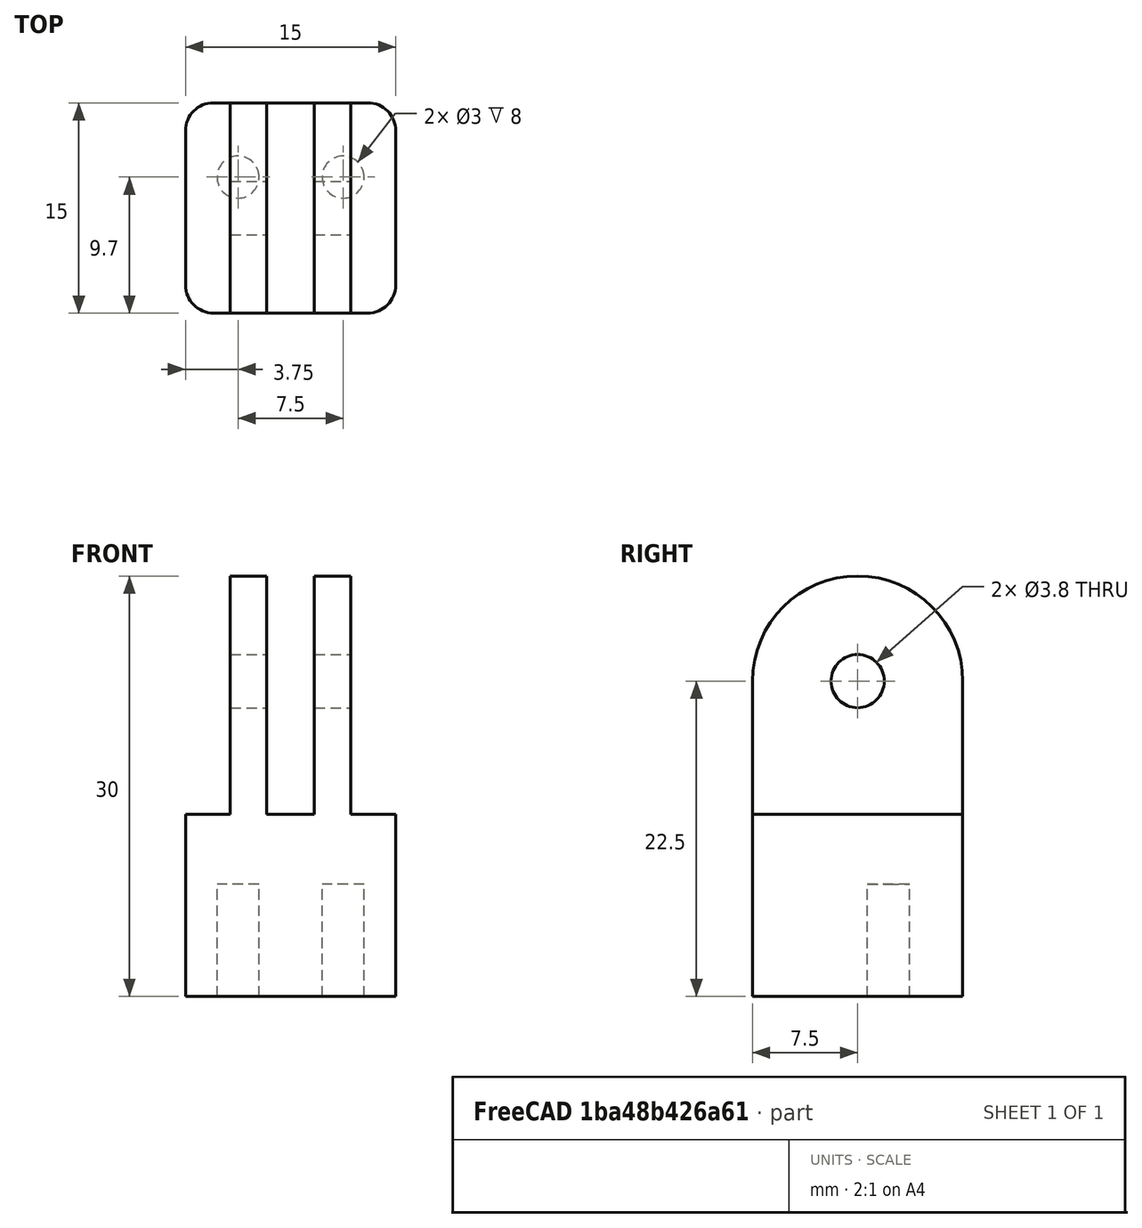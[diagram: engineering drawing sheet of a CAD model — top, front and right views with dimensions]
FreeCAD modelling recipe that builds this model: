
FCSTD DOCUMENT  (FreeCAD 0.19R23578 (Git))
Label: mag3110
License: FreeArt
LicenseURL: http://artlibre.org/licence/lal
objects: Spreadsheet::Sheet×1, Part::Cylinder×1, Part::FeaturePython×1, Part::Box×1, Part::Feature×1, Part::MultiFuse×1, Part::Cut×1, Part::Fillet×1, App::Part×1
note: 7 computed .brp shape members not serialized (recipe doc carries the construction recipe); baked Part::Feature solids carry a one-line shape summary decoded from their .brp

FEATURE [Spreadsheet::Sheet] Spreadsheet  label="p"
  cells = A1=pcb_x; B1(pcb_x)==13mm; A2=pcb_y; B2(pcb_y)==8mm; A3=pcb_z; B3(pcb_z)==1.7mm; A4=hole_dist_x; B4(hole_dist_x)==7.5mm; A5=hole_offset_y; B5(hole_offset_y)==2.7mm; A6=hole_r; B6(hole_r)==1.5mm; A7=stick_width; B7(stick_width)==15mm; A8=stick_length; B8(stick_length)==10mm
FEATURE [Part::Cylinder] Cylinder  label="bolt hole"
  Angle = 360
  AttacherType = Attacher::AttachEngine3D
  Height = 10
  Radius = 1.5
  expr: Radius = <<p>>.hole_r
FEATURE [Part::FeaturePython] Array  label="bolt hole array"  # Draft array (typed FeaturePython)
  Angle = 360
  ArrayType = 0
  Axis = (0,0,1)
  Base = -> Cylinder
  Center = (0,0,0)
  Fuse = false
  IntervalAxis = (0,0,0)
  IntervalX = (7.5,0,0)
  IntervalY = (0,1,0)
  IntervalZ = (0,0,1)
  NumberPolar = 1
  NumberX = 2
  NumberY = 1
  NumberZ = 1
  Placement = pos=(3.75,9.7,-2) rot=(0,0,1;0rad)
  expr: .Placement.Base.x = (<<p>>.stick_width - <<p>>.hole_dist_x) / 2
  expr: .IntervalX.x = <<p>>.hole_dist_x
  expr: .Placement.Base.y = <<p>>.stick_width - <<p>>.pcb_y + <<p>>.hole_offset_y
FEATURE [Part::Box] Box002  label="stick cube"
  AttacherType = Attacher::AttachEngine3D
  Height = 10
  Length = 15
  Width = 15
  expr: Length = <<p>>.stick_width
  expr: Width = <<p>>.stick_width
  expr: Height = <<p>>.stick_length
FEATURE [Part::Feature] Cut001001  label="side 2 cut001"
  Placement = pos=(7.5,7.5,10) rot=(0,0,1;1.5708rad)
  shape: bbox 15 x 15 x 20 mm, 16 faces (baked)
  expr: .Placement.Base.y = <<p>>.stick_width / 2
  expr: .Placement.Base.x = <<p>>.stick_width / 2
  expr: .Placement.Base.z = <<p>>.stick_length
FEATURE [Part::MultiFuse] Fusion  label="holder fusion"
  Shapes = -> [Box002,Cut001001]
FEATURE [Part::Cut] Cut  label="sensor cut"
  Base = -> Fusion
  Tool = -> Array
FEATURE [Part::Fillet] Fillet  label="sensor fillet"
  Base = -> Cut
  Edges = 8 edges r=2: [Edge1,Edge3,Edge6,Edge8,Edge10,Edge12,Edge18,Edge28]
FEATURE [App::Part] Part  label="mag3110 sensor part"
  Group = -> [Fillet]
  Origin = -> Origin
